# Revit family: K8
name_source: partatom
category: Lighting Fixtures
units: mm (PartAtom-declared; Revit-internal decimal feet)

## family parameters
Cut with Voids When Loaded = No
Host = Face
Light Source = Yes
OmniClass Number = 23.80.70.11
OmniClass Title = Luminaries for Internal Lighting
Part Type = Normal
Room Calculation Point = No
Round Connector Dimension = Use Diameter
Shared = Yes

## types (5) — shared parameters
Backbox = White
Ballast Factor = .95
Color Filter = 16777215
Default Elevation = 48.000"
Description = Heavy Duty Channel / 1 or 2-Lamp T8
Dimming Lamp Color Temperature Shift = <None>
Emit from Line Length = 44.000"
Glass = Glass
Lamp = 1
Manufacturer = Columbia Lighting
Model = K8
Tilt Angle = -90.00°
URL = https://www.currentlighting.com
Wattage Comments = 134W

## per-type parameters (varying)
| type | Photometric Web File |
| K8-196 | 11324.IES |
| K8-196HO | 8971.IES |
| K8-196VH0 | 11326.IES |
| K8-296 | 11325.IES |
| K8-296HO | 8973.IES |

## geometry (parser evidence)
native form markers: Sweep x2
no freeform markers — native parametric forms only
